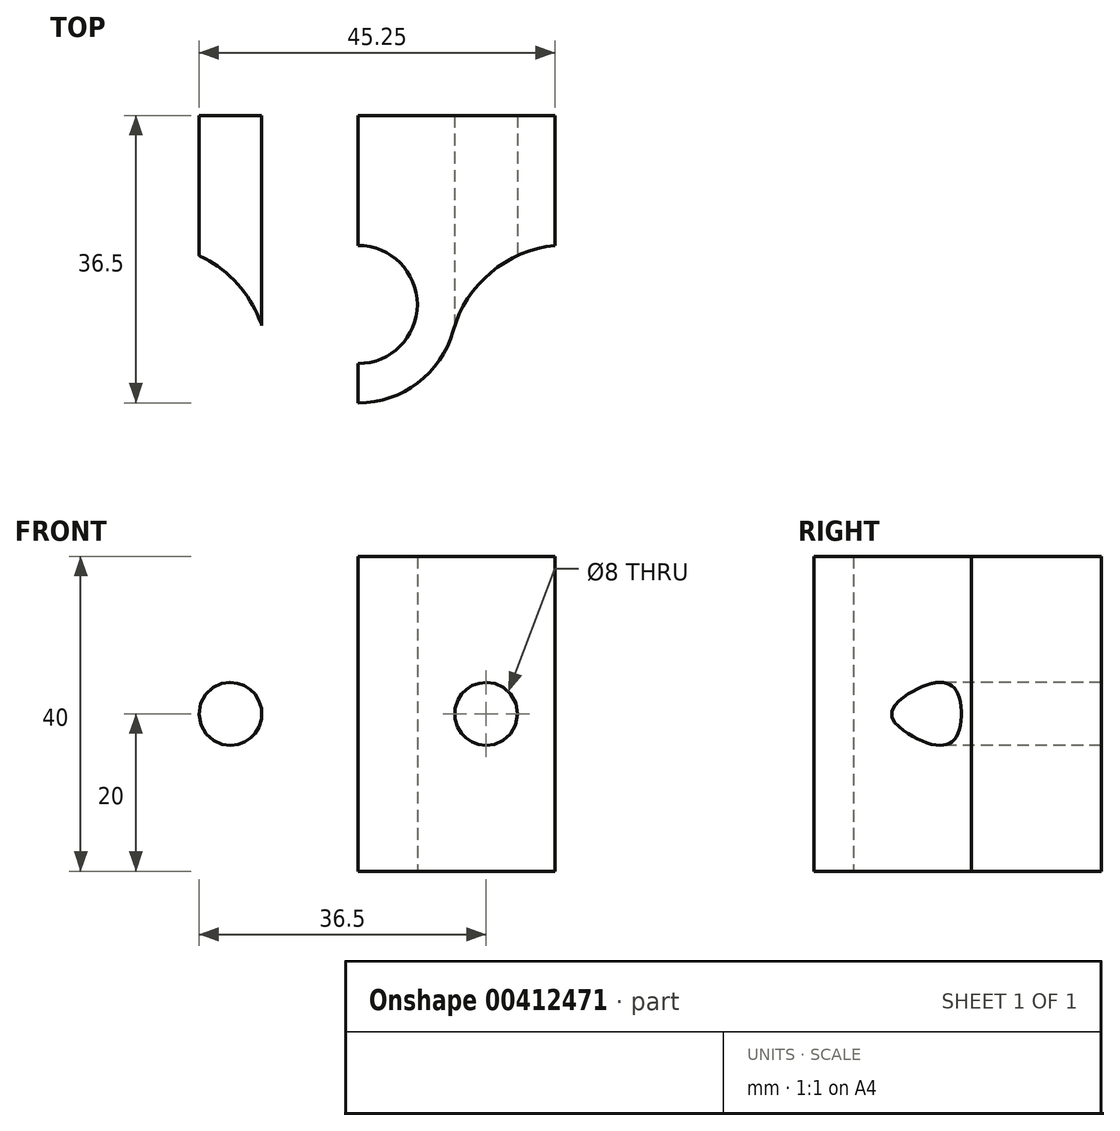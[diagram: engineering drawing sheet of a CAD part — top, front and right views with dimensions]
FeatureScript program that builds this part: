
annotation { "Feature Type Name" : "Feature", "Feature Type Description" : "" }
export const myFeature = defineFeature(function(context is Context, id is Id, definition is map)
    precondition{}
    {
        {
            var Q0;
            Q0=qCreatedBy(makeId("Top.planeOp"),FACE);
            var sketch = newSketch(context, id + "F0", { "sketchPlane" : qUnion([Q0])});
            skCircle(sketch, "E0", {"center": v(0, 0) * mm, "radius": 7.5 * mm});
            skCircle(sketch, "E1.0", {"center": v(0, 0) * mm, "radius": 12.5 * mm});
            skLineSegment(sketch, "E2.bottom", {"start": v(0, 7.5) * mm, "end": v(25, 7.5) * mm});
            skLineSegment(sketch, "E2.top", {"start": v(0, 24) * mm, "end": v(25, 24) * mm});
            skLineSegment(sketch, "E2.left", {"start": v(0, 7.5) * mm, "end": v(0, 24) * mm});
            skLineSegment(sketch, "E2.right", {"start": v(25, 7.5) * mm, "end": v(25, 24) * mm});
            skLineSegment(sketch, "E3.bottom", {"start": v(0, 7.5) * mm, "end": v(-25, 7.5) * mm});
            skLineSegment(sketch, "E3.top", {"start": v(0, 24) * mm, "end": v(-25, 24) * mm});
            skLineSegment(sketch, "E3.right", {"start": v(-25, 7.5) * mm, "end": v(-25, 24) * mm});
            skSolve(sketch);
        }
        {
            var Q0;
            {var subQ0=sQuery(id+"F0.wireOp",EDGE,"E0");Q0=makeQuery(id+"F0.imprint","IMPRINT",FACE,{"disambiguationData":[TD([[makeQuery(id+"F0.imprint","IMPRINT",EDGE,{"derivedFrom":subQ0}),-1.0]])]});}
            var Q1;
            {var subQ0=sQuery(id+"F0.wireOp",EDGE,"E2.left");Q1=makeQuery(id+"F0.imprint","IMPRINT",FACE,{"disambiguationData":[TD([[makeQuery(id+"F0.imprint","IMPRINT",EDGE,{"derivedFrom":subQ0}),-1.0]])]});}
            var Q2;
            {var subQ0=sQuery(id+"F0.wireOp",EDGE,"E2.top");Q2=makeQuery(id+"F0.imprint","IMPRINT",FACE,{"disambiguationData":[TD([[makeQuery(id+"F0.imprint","IMPRINT",EDGE,{"derivedFrom":subQ0}),-1.0]])]});}
            var Q3;
            {var subQ0=sQuery(id+"F0.wireOp",EDGE,"E3.top");Q3=makeQuery(id+"F0.imprint","IMPRINT",FACE,{"disambiguationData":[TD([[makeQuery(id+"F0.imprint","IMPRINT",EDGE,{"derivedFrom":subQ0}),1.0]])]});}
            var Q4;
            {var subQ0=sQuery(id+"F0.wireOp",EDGE,"E2.left");Q4=makeQuery(id+"F0.imprint","IMPRINT",FACE,{"disambiguationData":[TD([[makeQuery(id+"F0.imprint","IMPRINT",EDGE,{"derivedFrom":subQ0}),1.0]])]});}
            var Q5;
            {var subQ0=sQuery(id+"F0.wireOp",EDGE,"E2.left");Q5=makeQuery(id+"F0.imprint","IMPRINT",FACE,{"disambiguationData":[TD([[makeQuery(id+"F0.imprint","IMPRINT",EDGE,{"derivedFrom":subQ0}),-1.0]])]});}
            extrude(context, id + "F1", {"entities" : qUnion([Q0, Q1, Q2, Q3, Q4, Q5]), "depth" : 40 * mm});
        }
        {
            var Q0;
            Q0=makeQuery(id+"F1.opExtrude","SWEPT_EDGE",EDGE,{"disambiguationData":[OSD([sQuery(id+"F0.wireOp",EDGE,"E1.0"),sQuery(id+"F0.wireOp",EDGE,"E2.bottom")])]});
            var Q1;
            Q1=makeQuery(id+"F1.opExtrude","SWEPT_EDGE",EDGE,{"disambiguationData":[OSD([sQuery(id+"F0.wireOp",EDGE,"E1.0"),sQuery(id+"F0.wireOp",EDGE,"E3.bottom")])]});
            fillet(context, id + "F2", {"entities" : qUnion([Q0, Q1]), "radius" : 15 * mm, "tangentPropagation" : true, "allowEdgeOverflow" : false});
        }
        {
            var Q0;
            Q0=qCreatedBy(makeId("Front.planeOp"),FACE);
            var sketch = newSketch(context, id + "F3", { "sketchPlane" : qUnion([Q0])});
            skLineSegment(sketch, "E4.bottom", {"start": v(0, 0) * mm, "end": v(25, 0) * mm});
            skLineSegment(sketch, "E4.top", {"start": v(0, 40) * mm, "end": v(25, 40) * mm});
            skLineSegment(sketch, "E4.left", {"start": v(0, 0) * mm, "end": v(0, 40) * mm});
            skLineSegment(sketch, "E4.right", {"start": v(25, 0) * mm, "end": v(25, 40) * mm});
            skCircle(sketch, "E5", {"center": v(16.25, 20) * mm, "radius": 4 * mm});
            skLineSegment(sketch, "E6.MirrorCS", {"start": v(0, 40) * mm, "end": v(-25, 40) * mm});
            skLineSegment(sketch, "E7.MirrorCS", {"start": v(-25, 0) * mm, "end": v(-25, 40) * mm});
            skLineSegment(sketch, "E8.MirrorCS", {"start": v(0, 0) * mm, "end": v(-25, 0) * mm});
            skCircle(sketch, "E9.MirrorC", {"center": v(-16.25, 20) * mm, "radius": 4 * mm});
            skSolve(sketch);
        }
        {
            var Q0;
            Q0=makeQuery(id+"F3.imprint","IMPRINT",FACE,{"disambiguationData":[TD([[makeQuery(id+"F3.imprint","IMPRINT",EDGE,{"derivedFrom":sQuery(id+"F3.wireOp",EDGE,"E5")}),1.0]])]});
            var Q1;
            Q1=makeQuery(id+"F3.imprint","IMPRINT",FACE,{"disambiguationData":[TD([[makeQuery(id+"F3.imprint","IMPRINT",EDGE,{"derivedFrom":sQuery(id+"F3.wireOp",EDGE,"E9.MirrorC")}),-1.0]])]});
            extrude(context, id + "F4", {"entities" : qUnion([Q0, Q1]), "operationType" : NewBodyOperationType.REMOVE, "endBound" : BoundingType.SYMMETRIC, "oppositeDirection" : true, "depth" : 60 * mm});
        }
    });
